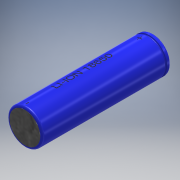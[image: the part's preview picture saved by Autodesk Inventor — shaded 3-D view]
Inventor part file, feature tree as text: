
AUTODESK INVENTOR PART (.ipt)
format: ipt  version: 2018 (Build 220112000, 112)  size: 605,184 bytes
history: native  units: mm
features: sketch x7, extrude x4, other x2, revolve x2, plane x2, fillet x1, pattern_circular x1
ambient origin geometry x8: Origin, YZ Plane, XZ Plane, XY Plane, X Axis, Y Axis, Z Axis, Center Point
bodies: Body1 (feature_tree)
feature tree (19):
  other  "Sólido1"
  extrude  "Extrusión1"  Depth=65.0mm TaperAngle=0.0deg
  revolve  "Revolución1"  [1 undecoded]
  fillet  "Empalme1"  [1 undecoded]
  plane  "Plano de trabajo1"
  extrude  "Extrusión2"  Depth=1.0mm
  revolve  "Revolución2"  [1 undecoded]
  extrude  "Extrusión4"  TaperAngle=90.0deg  [1 undecoded]
  pattern_circular  "Patrón circular1"  [2 undecoded]
  extrude  "Extrusión5"  Depth=1.0mm TaperAngle=0.0deg
  plane  "Plano de trabajo2"
  other  "Repujado1"
  sketch  "Boceto1"  dims[d0=18.0mm d1=65.0mm d2=0.0mm]
  sketch  "Boceto2"  dims[d3=1.0mm d4=2.5mm d5=90.0deg]
  sketch  "Boceto3"  dims[d6=1.0mm d7=1.0mm]
  sketch  "Boceto4"  dims[d8=7.0mm d9=0.1mm d10=0.0mm]
  sketch  "Boceto5"  dims[d11=0.1mm d12=90.0deg]
  sketch  "Boceto6"  dims[d13=1.2mm]
  sketch  "Boceto7"  dims[d14=2.5mm d15=6.8mm d18=1.0mm d19=0.0mm d20=60.0mm d21=360.0deg d23=0.1mm d24=0.0mm d25=0.1mm d26=0.0mm]
note: 6 required parameter values undecoded (feature->parameter linkage not recoverable at this tier; creation-order binding heuristic only, values carry confidence <= 0.55)